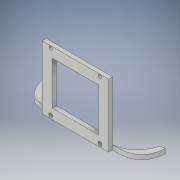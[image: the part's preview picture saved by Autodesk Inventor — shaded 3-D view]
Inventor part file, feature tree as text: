
AUTODESK INVENTOR PART (.ipt)
format: ipt  version: 2019 (Build 230136000, 136)  size: 211,968 bytes
history: native  units: mm
features: sketch x6, other x3, extrude x3, mirror x2, loft x1, projected_geometry x1
ambient origin geometry x8: Origin, YZ Plane, XZ Plane, XY Plane, X Axis, Y Axis, Z Axis, Center Point
bodies: Body1 (feature_tree)
feature tree (16):
  other  "Bryła1"
  sketch  "Szkic1"
  other  "Płaszczyzna konstrukcyjna2"
  other  "Płaszczyzna konstrukcyjna3"
  sketch  "Szkic3"
  sketch  "Szkic4"
  sketch  "Szkic5"
  loft  "Wyciągnięcie złożone1"
  extrude  "Wyciągnięcie proste1"  Depth=4.5mm
  mirror  "Odbij1"
  sketch  "Szkic10"
  extrude  "Wyciągnięcie proste3"  Depth=20.0mm
  extrude  "Wyciągnięcie proste4"  TaperAngle=0.0deg  [1 undecoded]
  mirror  "Odbij2"
  projected_geometry  "Pętla rzutowana3"
  sketch  "Szkic11"
note: 1 required parameter value undecoded (feature->parameter linkage not recoverable at this tier; creation-order binding heuristic only, values carry confidence <= 0.55)
